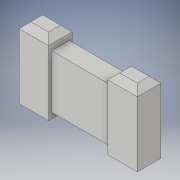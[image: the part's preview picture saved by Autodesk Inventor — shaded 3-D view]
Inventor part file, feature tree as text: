
AUTODESK INVENTOR PART (.ipt)
format: ipt  version: 2019 (Build 230136000, 136)  size: 153,088 bytes
history: native  units: mm
features: extrude x4, sketch x4, chamfer x3, plane x2
ambient origin geometry x8: Origin, YZ Plane, XZ Plane, XY Plane, X Axis, Y Axis, Z Axis, Center Point
bodies: Solid1 (feature_tree)
feature tree (13):
  extrude  "Extrusion1"  Depth=1.0mm TaperAngle=0.0deg
  plane  "Work Plane1"
  extrude  "Extrusion2"  [1 undecoded]
  plane  "Work Plane2"
  extrude  "Extrusion3"  Depth=0.5mm
  chamfer  "Chamfer1"  Distance=1.2mm
  chamfer  "Chamfer2"  Distance=0.4mm
  chamfer  "Chamfer3"  Distance=0.1mm Angle=45.0deg
  extrude  "Extrusion4"  Depth=0.1mm TaperAngle=45.0deg
  sketch  "Sketch1"  dims[d0=2.0mm d1=1.0mm d2=0.0mm]
  sketch  "Sketch3"  dims[d3=0.3mm d6=-0.5mm]
  sketch  "Sketch4"  dims[d7=0.5mm d8=0.5mm d9=1.2mm d10=0.0mm]
  sketch  "Sketch5"  dims[d11=-0.15mm d12=0.4mm d13=0.0mm d14=0.1mm d15=2.0mm d16=45.0deg d17=0.1mm d18=2.0mm d19=45.0deg d20=0.1mm d21=2.0mm d22=45.0deg d23=0.1mm d24=0.0mm]
note: 1 required parameter value undecoded (feature->parameter linkage not recoverable at this tier; creation-order binding heuristic only, values carry confidence <= 0.55)
